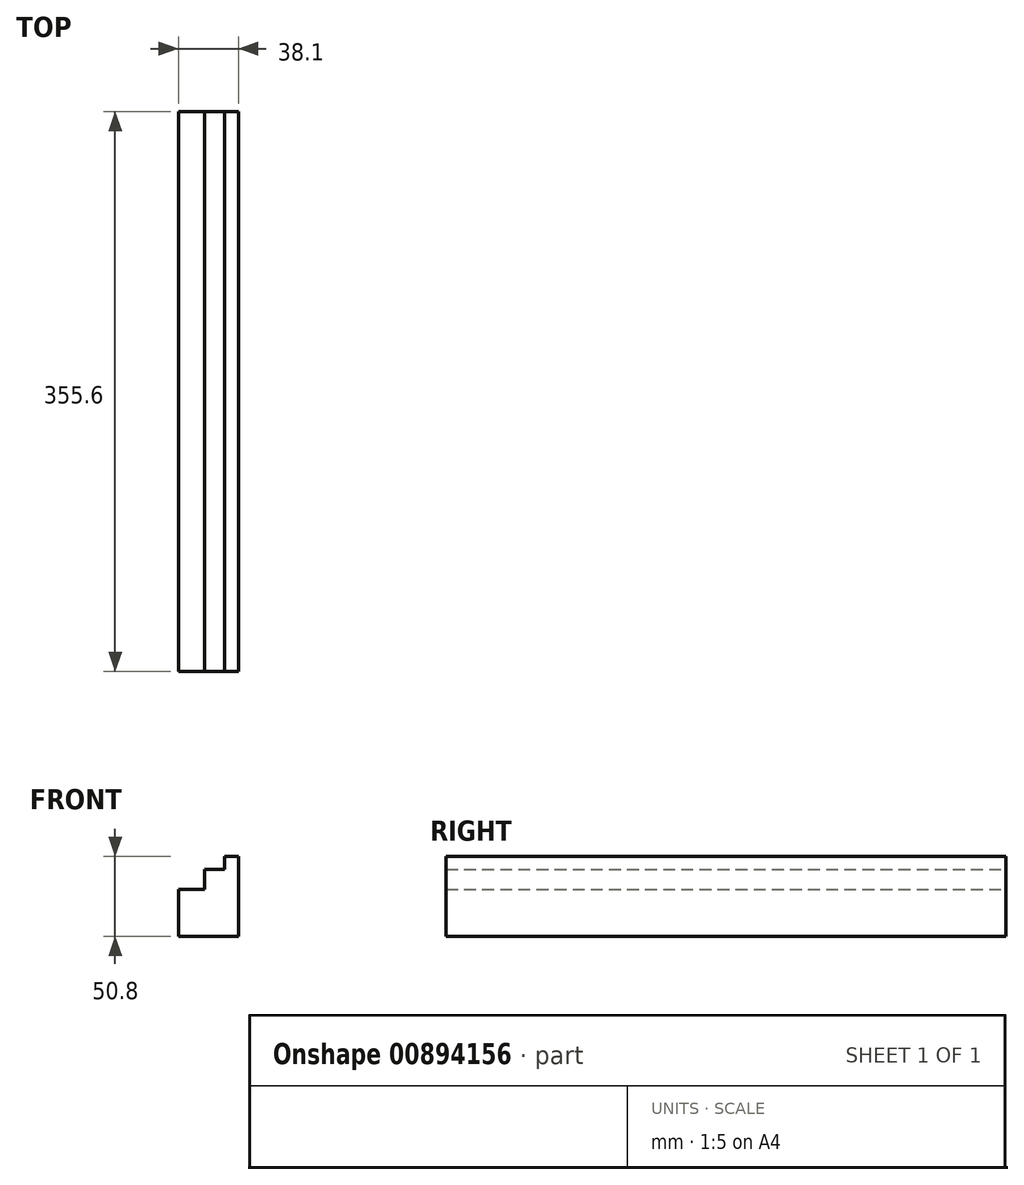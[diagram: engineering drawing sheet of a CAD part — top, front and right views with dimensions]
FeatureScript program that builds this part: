
annotation { "Feature Type Name" : "Feature", "Feature Type Description" : "" }
export const myFeature = defineFeature(function(context is Context, id is Id, definition is map)
    precondition{}
    {
        {
            var Q0;
            Q0=qCreatedBy(makeId("Front.planeOp"),FACE);
            var sketch = newSketch(context, id + "F0", { "sketchPlane" : qUnion([Q0])});
            skLineSegment(sketch, "E0.bottom", {"start": v(38.1, 0) * mm, "end": v(0, 0) * mm});
            skLineSegment(sketch, "E0.top", {"start": v(38.1, 50.8) * mm, "end": v(29.21, 50.8) * mm});
            skLineSegment(sketch, "E0.left", {"start": v(38.1, 0) * mm, "end": v(38.1, 50.8) * mm});
            skLineSegment(sketch, "E0.right", {"start": v(0, 0) * mm, "end": v(0, 29.85) * mm});
            skLineSegment(sketch, "E1.bottom", {"start": v(0, 29.85) * mm, "end": v(16.51, 29.85) * mm});
            skLineSegment(sketch, "E1.right", {"start": v(16.51, 29.85) * mm, "end": v(16.51, 42.55) * mm});
            skLineSegment(sketch, "E2.bottom", {"start": v(16.51, 42.55) * mm, "end": v(29.21, 42.55) * mm});
            skLineSegment(sketch, "E2.right", {"start": v(29.21, 42.55) * mm, "end": v(29.21, 50.8) * mm});
            skPoint(sketch, "E3.orphan", {"position": v(0, 59.7) * mm});
            skSolve(sketch);
        }
        {
            var Q0;
            Q0 = qSketchRegion(id + "F0", true);
            extrude(context, id + "F1", {"entities" : qUnion([Q0]), "depth" : 355.6 * mm, "offsetDistance" : 25.4 * mm});
        }
    });
